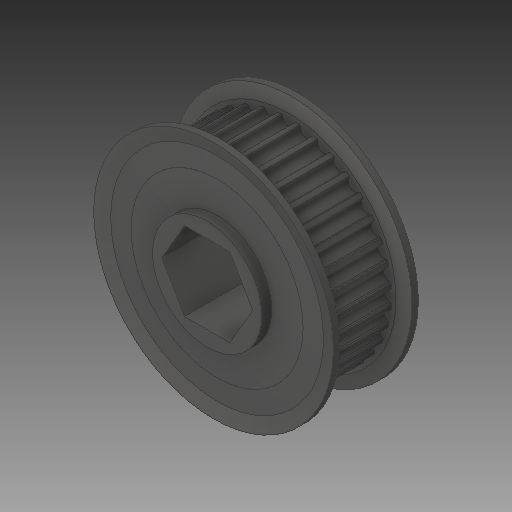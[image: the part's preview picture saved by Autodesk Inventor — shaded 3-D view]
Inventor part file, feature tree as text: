
AUTODESK INVENTOR PART (.ipt)
format: ipt  version: 2018 (Build 220112000, 112)  size: 430,080 bytes
history: native  units: in
note: dims shown in document units (in); Inventor stores cm internally (conversion verified against a paired STEP export)
features: revolve x2, other x1
ambient origin geometry x8: Origin, YZ Plane, XZ Plane, XY Plane, X Axis, Y Axis, Z Axis, Center Point
bodies: Solid1 (feature_tree), Solid2 (feature_tree), Solid3 (feature_tree)
feature tree (3):
  revolve  "Revolve1[1]"  [1 undecoded]
  revolve  "Revolve1[2]"  [1 undecoded]
  other  "Cut-Extrude4"
note: 2 required parameter values undecoded (feature->parameter linkage not recoverable at this tier; creation-order binding heuristic only, values carry confidence <= 0.55)
